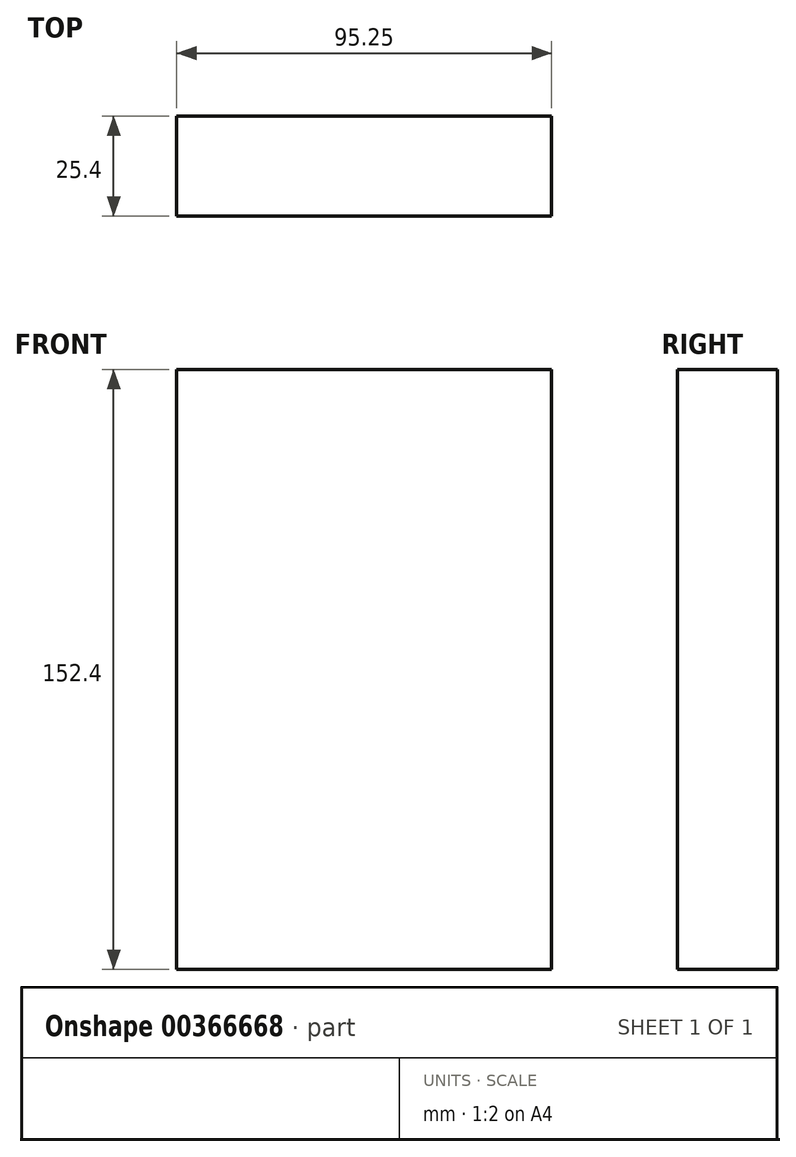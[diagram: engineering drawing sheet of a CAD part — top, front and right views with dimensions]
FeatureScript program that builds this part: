
annotation { "Feature Type Name" : "Feature", "Feature Type Description" : "" }
export const myFeature = defineFeature(function(context is Context, id is Id, definition is map)
    precondition{}
    {
        {
            var Q0;
            Q0=qCreatedBy(makeId("Front.planeOp"),FACE);
            var sketch = newSketch(context, id + "F0", { "sketchPlane" : qUnion([Q0])});
            skLineSegment(sketch, "E0.bottom", {"start": v(-95.25, 152.4) * mm, "end": v(0, 152.4) * mm});
            skLineSegment(sketch, "E0.top", {"start": v(-95.25, 0) * mm, "end": v(0, 0) * mm});
            skLineSegment(sketch, "E0.left", {"start": v(-95.25, 152.4) * mm, "end": v(-95.25, 0) * mm});
            skLineSegment(sketch, "E0.right", {"start": v(0, 152.4) * mm, "end": v(0, 0) * mm});
            skSolve(sketch);
        }
        {
            var Q0;
            Q0=makeQuery(id+"F0.imprint","IMPRINT",FACE,{"disambiguationData":[TD([[makeQuery(id+"F0.imprint","IMPRINT",EDGE,{"derivedFrom":sQuery(id+"F0.wireOp",EDGE,"E0.bottom")}),-1.0]])]});
            extrude(context, id + "F1", {"entities" : qUnion([Q0]), "depth" : 25.4 * mm});
        }
    });
